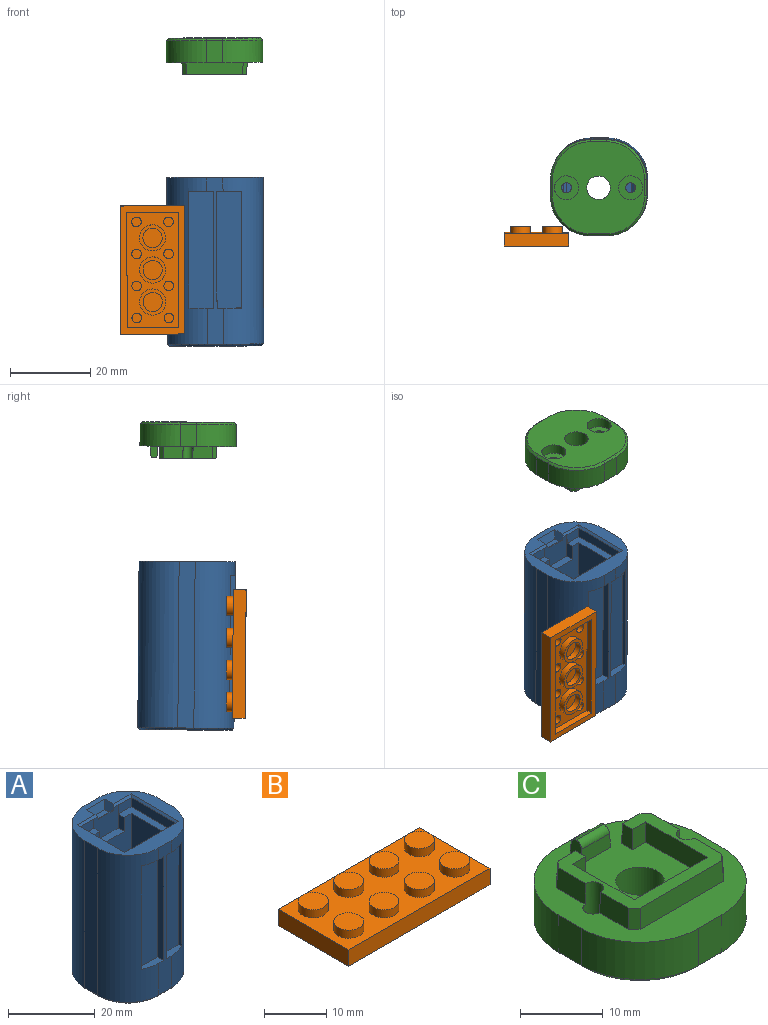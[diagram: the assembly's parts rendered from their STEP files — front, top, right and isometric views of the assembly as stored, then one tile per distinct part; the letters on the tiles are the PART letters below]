
ASSEMBLY  parts=3 mates=3
PART A: 128 faces, bbox 24x24x42 mm
  f0: plane 5.98x0.52mm, normal (0,-0.69,0.72), area 4mm2, adj f1,f112,f116,f118,f124
  f1: plane 24x24mm, normal (0,0,1), area 202.4mm2, adj f0,f2,f8,f9,f10,f13,f14,f15
  f2: plane 5.98x0.52mm, normal (0,-0.69,0.72), area 4mm2, adj f1,f4,f115,f118,f122
  f3: plane 27x12.5mm, normal (0,-1,0), area 305.5mm2, adj f5,f6,f53,f110,f119,f120,f121
  f4: plane 4.23x2.5mm, normal (0,-1,0.03), area 10.5mm2, adj f2,f110,f111,f120
  f5: plane 27x10.5mm, normal (-1,0,0), area 283.5mm2, adj f3,f7,f53,f110
  f6: plane 27x10.5mm, normal (1,0,0), area 283.5mm2, adj f3,f7,f53,f110
  f7: plane 27x12.5mm, normal (0,1,0), area 337.5mm2, adj f5,f6,f53,f110
  f8: plane 41.5x4mm, normal (0,-1,0), area 72.6mm2, adj f1,f9,f10,f57,f100,f101,f103,f105
  f9: cylinder r=10mm len=41.5mm, axis (0,0,-1), area 512.3mm2, adj f1,f8,f13,f59,f105,f106,f107
  f10: cylinder r=10mm len=41.5mm, axis (0,0,-1), area 512.3mm2, adj f1,f8,f17,f55,f100,f101,f102
  f11: cylinder r=2.65mm len=5.6mm, axis (0,0,-1), area 93.2mm2, adj f90,f98
  f12: cylinder r=2.65mm len=5.6mm, axis (0,0,-1), area 93.2mm2, adj f86,f99
  f13: plane 41.5x4mm, normal (1,0,0), area 166mm2, adj f1,f9,f14,f61
  f14: cylinder r=10mm len=41.5mm, axis (0,0,-1), area 651.9mm2, adj f1,f13,f15,f60
  f15: plane 41.5x4mm, normal (0,1,0), area 166mm2, adj f1,f14,f16,f58
  f16: cylinder r=10mm len=41.5mm, axis (0,0,-1), area 651.9mm2, adj f1,f15,f17,f56
  f17: plane 41.5x4mm, normal (-1,0,0), area 166mm2, adj f1,f10,f16,f54
  f18: plane 23x23mm, normal (0,0,-1), area 261.8mm2, adj f54,f55,f56,f57,f58,f59,f60,f61
  f19: cylinder r=0.1mm len=8.53mm, axis (0,0,-1), area 1.3mm2, adj f20,f34,f35,f80,f81
  f20: plane 8.5x1.21mm, normal (0,1,0), area 10.3mm2, adj f19,f21,f35,f80
  f21: cylinder r=2.65mm len=8.5mm, axis (0,0,-1), area 19.3mm2, adj f20,f22,f35,f62
  f22: plane 8.5x1.21mm, normal (0,-1,0), area 10.3mm2, adj f21,f23,f35,f85
  f23: cylinder r=0.1mm len=8.53mm, axis (0,0,-1), area 1.3mm2, adj f22,f24,f35,f84,f85
  f24: plane 8.5x1.21mm, normal (-1,0,0), area 10.3mm2, adj f23,f25,f35,f84
  f25: cylinder r=2.65mm len=8.5mm, axis (0,0,-1), area 19.3mm2, adj f24,f26,f35,f63
  f26: plane 8.5x1.21mm, normal (1,0,0), area 10.3mm2, adj f25,f27,f35,f82
  f27: cylinder r=0.1mm len=8.53mm, axis (0,0,-1), area 1.3mm2, adj f26,f28,f35,f82,f83
  f28: plane 8.5x1.21mm, normal (0,-1,0), area 10.3mm2, adj f27,f29,f35,f83
  f29: cylinder r=2.65mm len=8.5mm, axis (0,0,-1), area 19.3mm2, adj f28,f30,f35,f69
  f30: plane 8.5x1.21mm, normal (0,1,0), area 10.3mm2, adj f29,f31,f35,f78
  f31: cylinder r=0.1mm len=8.53mm, axis (0,0,-1), area 1.3mm2, adj f30,f32,f35,f78,f79
  f32: plane 8.5x1.21mm, normal (1,0,0), area 10.3mm2, adj f31,f33,f35,f79
  f33: cylinder r=2.65mm len=8.5mm, axis (0,0,-1), area 19.3mm2, adj f32,f34,f35,f64
  f34: plane 8.5x1.21mm, normal (-1,0,0), area 10.3mm2, adj f19,f33,f35,f81
  f35: plane 5.3x5.3mm, normal (0,0,-1), area 17.8mm2, adj f19,f20,f21,f22,f23,f24,f25,f26
  f36: cylinder r=0.1mm len=8.53mm, axis (0,0,-1), area 1.3mm2, adj f37,f51,f52,f72,f73
  f37: plane 8.5x1.21mm, normal (0,1,0), area 10.3mm2, adj f36,f38,f52,f73
  f38: cylinder r=2.65mm len=8.5mm, axis (0,0,-1), area 19.3mm2, adj f37,f39,f52,f68
  f39: plane 8.5x1.21mm, normal (0,-1,0), area 10.3mm2, adj f38,f40,f52,f71
  f40: cylinder r=0.1mm len=8.53mm, axis (0,0,-1), area 1.3mm2, adj f39,f41,f52,f70,f71
  f41: plane 8.5x1.21mm, normal (-1,0,0), area 10.3mm2, adj f40,f42,f52,f70
  f42: cylinder r=2.65mm len=8.5mm, axis (0,0,-1), area 19.3mm2, adj f41,f43,f52,f67
  f43: plane 8.5x1.21mm, normal (1,0,0), area 10.3mm2, adj f42,f44,f52,f76
  f44: cylinder r=0.1mm len=8.53mm, axis (0,0,-1), area 1.3mm2, adj f43,f45,f52,f76,f77
  f45: plane 8.5x1.21mm, normal (0,-1,0), area 10.3mm2, adj f44,f46,f52,f77
  f46: cylinder r=2.65mm len=8.5mm, axis (0,0,-1), area 19.3mm2, adj f45,f47,f52,f66
  f47: plane 8.5x1.21mm, normal (0,1,0), area 10.3mm2, adj f46,f48,f52,f74
  f48: cylinder r=0.1mm len=8.53mm, axis (0,0,-1), area 1.3mm2, adj f47,f49,f52,f74,f75
  f49: plane 8.5x1.21mm, normal (1,0,0), area 10.3mm2, adj f48,f50,f52,f75
  f50: cylinder r=2.65mm len=8.5mm, axis (0,0,-1), area 19.3mm2, adj f49,f51,f52,f65
  f51: plane 8.5x1.21mm, normal (-1,0,0), area 10.3mm2, adj f36,f50,f52,f72
  f52: plane 5.3x5.3mm, normal (0,0,-1), area 17.8mm2, adj f36,f37,f38,f39,f40,f41,f42,f43
  f53: plane 12.5x10.5mm, normal (0,0,1), area 63.3mm2, adj f3,f5,f6,f7,f97
  f54: plane 4x0.5mm, normal (-0.71,0,-0.71), area 2.8mm2, adj f17,f18,f55,f56
  f55: cone r=10mm half-angle=45deg, axis (0,0,1), area 10.8mm2, adj f10,f18,f54,f57
  f56: cone r=10mm half-angle=45deg, axis (0,0,1), area 10.8mm2, adj f16,f18,f54,f58
  f57: plane 4x0.5mm, normal (0,-0.71,-0.71), area 2.8mm2, adj f8,f18,f55,f59,f98
  f58: plane 4x0.5mm, normal (0,0.71,-0.71), area 2.8mm2, adj f15,f18,f56,f60,f99
  f59: cone r=10mm half-angle=45deg, axis (0,0,1), area 10.8mm2, adj f9,f18,f57,f61
  f60: cone r=10mm half-angle=45deg, axis (0,0,1), area 10.8mm2, adj f14,f18,f58,f61
  f61: plane 4x0.5mm, normal (0.71,0,-0.71), area 2.8mm2, adj f13,f18,f59,f60
  f62: cone r=2.65mm half-angle=45deg, axis (0,0,-1), area 2mm2, adj f18,f21,f80,f85
  f63: cone r=2.65mm half-angle=45deg, axis (0,0,-1), area 2mm2, adj f18,f25,f82,f84
  f64: cone r=2.65mm half-angle=45deg, axis (0,0,-1), area 2mm2, adj f18,f33,f79,f81
  f65: cone r=3.15mm half-angle=45deg, axis (0,0,-1), area 2mm2, adj f18,f50,f72,f75
  f66: cone r=3.15mm half-angle=45deg, axis (0,0,-1), area 2mm2, adj f18,f46,f74,f77
  f67: cone r=3.15mm half-angle=45deg, axis (0,0,-1), area 2mm2, adj f18,f42,f70,f76
  f68: cone r=3.15mm half-angle=45deg, axis (0,0,-1), area 2mm2, adj f18,f38,f71,f73
  f69: cone r=2.65mm half-angle=45deg, axis (0,0,-1), area 2mm2, adj f18,f29,f78,f83
  f70: plane 1.6x0.51mm, normal (-0.71,0,-0.71), area 0.9mm2, adj f18,f40,f41,f67,f71
  f71: plane 1.6x0.51mm, normal (0,-0.71,-0.71), area 0.9mm2, adj f18,f39,f40,f68,f70
  f72: plane 1.6x0.51mm, normal (-0.71,0,-0.71), area 0.9mm2, adj f18,f36,f51,f65,f73
  f73: plane 1.6x0.51mm, normal (0,0.71,-0.71), area 0.9mm2, adj f18,f36,f37,f68,f72
  f74: plane 1.6x0.51mm, normal (0,0.71,-0.71), area 0.9mm2, adj f18,f47,f48,f66,f75
  f75: plane 1.6x0.51mm, normal (0.71,0,-0.71), area 0.9mm2, adj f18,f48,f49,f65,f74
  f76: plane 1.6x0.51mm, normal (0.71,0,-0.71), area 0.9mm2, adj f18,f43,f44,f67,f77
  f77: plane 1.6x0.51mm, normal (0,-0.71,-0.71), area 0.9mm2, adj f18,f44,f45,f66,f76
  f78: plane 1.6x0.51mm, normal (0,0.71,-0.71), area 0.9mm2, adj f18,f30,f31,f69,f79
  f79: plane 1.6x0.51mm, normal (0.71,0,-0.71), area 0.9mm2, adj f18,f31,f32,f64,f78
  f80: plane 1.6x0.51mm, normal (0,0.71,-0.71), area 0.9mm2, adj f18,f19,f20,f62,f81
  f81: plane 1.6x0.51mm, normal (-0.71,0,-0.71), area 0.9mm2, adj f18,f19,f34,f64,f80
  f82: plane 1.6x0.51mm, normal (0.71,0,-0.71), area 0.9mm2, adj f18,f26,f27,f63,f83
  f83: plane 1.6x0.51mm, normal (0,-0.71,-0.71), area 0.9mm2, adj f18,f27,f28,f69,f82
  f84: plane 1.6x0.51mm, normal (-0.71,0,-0.71), area 0.9mm2, adj f18,f23,f24,f63,f85
  f85: plane 1.6x0.51mm, normal (0,-0.71,-0.71), area 0.9mm2, adj f18,f22,f23,f62,f84
  f86: plane 6.7x6.7mm, normal (0,0,1), area 13.2mm2, adj f12,f87
  f87: cylinder r=3.35mm len=6.7mm, axis (0,0,-1), area 10.5mm2, adj f86,f96
  f88: plane 5.3x5.3mm, normal (0,0,-1), area 22.1mm2, adj f89
  f89: cylinder r=2.65mm len=5.3mm, axis (0,0,-1), area 21.6mm2, adj f88,f96
  f90: plane 6.7x6.7mm, normal (0,0,1), area 13.2mm2, adj f11,f91
  f91: cylinder r=3.35mm len=6.7mm, axis (0,0,-1), area 10.5mm2, adj f90,f95
  f92: plane 5.3x5.3mm, normal (0,0,-1), area 22.1mm2, adj f93
  f93: cylinder r=2.65mm len=5.3mm, axis (0,0,-1), area 21.6mm2, adj f92,f95
  f94: cylinder r=4.15mm len=11.5mm, axis (0,0,-1), area 299.9mm2, adj f18,f97
  f95: cone r=2.35mm half-angle=45deg, axis (0,0,-1), area 18.7mm2, adj f91,f93
  f96: cone r=3.35mm half-angle=45deg, axis (0,0,-1), area 18.7mm2, adj f87,f89
  f97: cone r=4.65mm half-angle=45deg, axis (0,0,1), area 19.5mm2, adj f53,f94
  f98: cone r=2.65mm half-angle=45deg, axis (0,0,-1), area 24.8mm2, adj f11,f18,f57
  f99: cone r=2.65mm half-angle=45deg, axis (0,0,-1), area 24.8mm2, adj f12,f18,f58
  f100: plane 6.2x2mm, normal (0,0,1), area 10.7mm2, adj f8,f10,f102,f103,f104
  f101: plane 6.2x2mm, normal (0,0,-1), area 10.7mm2, adj f8,f10,f102,f103,f104
  f102: plane 29.2x0.88mm, normal (1,0,0), area 25.7mm2, adj f10,f100,f101,f104
  f103: plane 29.2x2mm, normal (-1,0,0), area 58.4mm2, adj f8,f100,f101,f104
  f104: plane 29.2x6.2mm, normal (0,-1,0), area 181mm2, adj f100,f101,f102,f103
  f105: plane 6.2x2mm, normal (0,0,-1), area 10.7mm2, adj f8,f9,f107,f108,f109
  f106: plane 6.2x2mm, normal (0,0,1), area 10.7mm2, adj f8,f9,f107,f108,f109
  f107: plane 29.2x0.88mm, normal (-1,0,0), area 25.7mm2, adj f9,f105,f106,f109
  f108: plane 29.2x2mm, normal (1,0,0), area 58.4mm2, adj f8,f105,f106,f109
  f109: plane 29.2x6.2mm, normal (0,-1,0), area 181mm2, adj f105,f106,f107,f108
  f110: plane 16.29x14.29mm, normal (0,0,1), area 86.4mm2, adj f3,f4,f5,f6,f7,f111,f112,f113
  f111: plane 14.47x2.5mm, normal (-1,0,0.03), area 36mm2, adj f4,f110,f114,f115
  f112: plane 4.23x2.5mm, normal (0,-1,0.03), area 10.5mm2, adj f0,f110,f113,f119
  f113: plane 14.47x2.5mm, normal (1,0,0.03), area 36mm2, adj f110,f112,f114,f116
  f114: plane 16.47x2.5mm, normal (0,1,0.03), area 41mm2, adj f110,f111,f113,f117
  f115: plane 15.5x0.52mm, normal (-0.69,0,0.72), area 10.8mm2, adj f1,f2,f111,f117
  f116: plane 15.5x0.52mm, normal (0.69,0,0.72), area 10.8mm2, adj f0,f1,f113,f117
  f117: plane 17.5x0.52mm, normal (0,0.69,0.72), area 12.2mm2, adj f1,f114,f115,f116
  f118: plane 8x6.5mm, normal (0,-1,0), area 48.1mm2, adj f0,f2,f119,f120,f121,f122,f124,f127
  f119: plane 6.5x1.98mm, normal (1,0,0), area 8mm2, adj f3,f110,f112,f118,f121
  f120: plane 6.5x1.98mm, normal (-1,0,0), area 8mm2, adj f3,f4,f110,f118,f121
  f121: plane 8x1.98mm, normal (0,0,1), area 15.9mm2, adj f3,f118,f119,f120
  f122: plane 3.27x2mm, normal (-0.91,0,0.42), area 5.7mm2, adj f1,f2,f118,f123,f125,f126,f127
  f123: plane 6x2mm, normal (0,-0.91,0.42), area 11.2mm2, adj f1,f122,f124,f126
  f124: plane 3.27x2mm, normal (0.91,0,0.42), area 5.7mm2, adj f0,f1,f118,f123,f125,f126,f127
  f125: plane 4.35x0.23mm, normal (0,0.91,0.42), area 1.1mm2, adj f122,f124,f126,f127
  f126: plane 4.13x1.63mm, normal (0,0,1), area 6.8mm2, adj f122,f123,f124,f125
  f127: cylinder r=1mm len=4.84mm, axis (1,0,0), area 3.8mm2, adj f118,f122,f124,f125
PART B: 55 faces, bbox 32x16x4.8 mm
  f0: plane 4.8x4.8mm, normal (0,0,-1), area 18.1mm2, adj f2
  f1: plane 4.8x4.8mm, normal (0,0,-1), area 18.1mm2, adj f5
  f2: cylinder r=2.4mm len=4.8mm, axis (0,0,1), area 24.1mm2, adj f0,f4
  f3: cylinder r=3.26mm len=6.51mm, axis (0,0,1), area 32.7mm2, adj f4,f18
  f4: plane 6.51x6.51mm, normal (0,0,-1), area 15.2mm2, adj f2,f3
  f5: cylinder r=2.4mm len=4.8mm, axis (0,0,1), area 24.1mm2, adj f1,f7
  f6: cylinder r=3.26mm len=6.51mm, axis (0,0,1), area 32.7mm2, adj f7,f18
  f7: plane 6.51x6.51mm, normal (0,0,-1), area 15.2mm2, adj f5,f6
  f8: plane 32x16mm, normal (0,0,-1), area 143.4mm2, adj f9,f10,f11,f12,f14,f15,f16,f17
  f9: plane 16x3.2mm, normal (-1,0,0), area 51.2mm2, adj f8,f10,f12,f13
  f10: plane 32x3.2mm, normal (0,-1,0), area 102.4mm2, adj f8,f9,f11,f13
  f11: plane 16x3.2mm, normal (1,0,0), area 51.2mm2, adj f8,f10,f12,f13
  f12: plane 32x3.2mm, normal (0,1,0), area 102.4mm2, adj f8,f9,f11,f13
  f13: plane 32x16mm, normal (0,0,1), area 367.2mm2, adj f9,f10,f11,f12,f19,f21,f23,f25
  f14: plane 12.8x1.6mm, normal (1,0,0), area 20.5mm2, adj f8,f15,f17,f18
  f15: plane 28.8x1.6mm, normal (0,-1,0), area 46.1mm2, adj f8,f14,f16,f18
  f16: plane 12.8x1.6mm, normal (-1,0,0), area 20.5mm2, adj f8,f15,f17,f18
  f17: plane 28.8x1.6mm, normal (0,1,0), area 46.1mm2, adj f8,f14,f16,f18
  f18: plane 28.8x12.8mm, normal (0,0,-1), area 232.5mm2, adj f3,f6,f14,f15,f16,f17,f35,f37
  f19: cylinder r=2.4mm len=4.8mm, axis (0,0,-1), area 24.1mm2, adj f13,f20
  f20: plane 4.8x4.8mm, normal (0,0,1), area 18.1mm2, adj f19
  f21: cylinder r=2.4mm len=4.8mm, axis (0,0,-1), area 24.1mm2, adj f13,f22
  f22: plane 4.8x4.8mm, normal (0,0,1), area 18.1mm2, adj f21
  f23: cylinder r=2.4mm len=4.8mm, axis (0,0,-1), area 24.1mm2, adj f13,f24
  f24: plane 4.8x4.8mm, normal (0,0,1), area 18.1mm2, adj f23
  f25: cylinder r=2.4mm len=4.8mm, axis (0,0,-1), area 24.1mm2, adj f13,f26
  f26: plane 4.8x4.8mm, normal (0,0,1), area 18.1mm2, adj f25
  f27: cylinder r=2.4mm len=4.8mm, axis (0,0,-1), area 24.1mm2, adj f13,f28
  f28: plane 4.8x4.8mm, normal (0,0,1), area 18.1mm2, adj f27
  f29: cylinder r=2.4mm len=4.8mm, axis (0,0,-1), area 24.1mm2, adj f13,f30
  f30: plane 4.8x4.8mm, normal (0,0,1), area 18.1mm2, adj f29
  f31: cylinder r=2.4mm len=4.8mm, axis (0,0,-1), area 24.1mm2, adj f13,f32
  f32: plane 4.8x4.8mm, normal (0,0,1), area 18.1mm2, adj f31
  f33: cylinder r=2.4mm len=4.8mm, axis (0,0,-1), area 24.1mm2, adj f13,f34
  f34: plane 4.8x4.8mm, normal (0,0,1), area 18.1mm2, adj f33
  f35: cylinder r=1.2mm len=2.4mm, axis (0,0,-1), area 12.1mm2, adj f18,f36
  f36: plane 2.4x2.4mm, normal (0,0,-1), area 4.5mm2, adj f35
  f37: cylinder r=1.2mm len=2.4mm, axis (0,0,-1), area 12.1mm2, adj f18,f38
  f38: plane 2.4x2.4mm, normal (0,0,-1), area 4.5mm2, adj f37
  f39: cylinder r=1.2mm len=2.4mm, axis (0,0,-1), area 12.1mm2, adj f18,f40
  f40: plane 2.4x2.4mm, normal (0,0,-1), area 4.5mm2, adj f39
  f41: cylinder r=1.2mm len=2.4mm, axis (0,0,-1), area 12.1mm2, adj f18,f42
  f42: plane 2.4x2.4mm, normal (0,0,-1), area 4.5mm2, adj f41
  f43: cylinder r=1.2mm len=2.4mm, axis (0,0,-1), area 12.1mm2, adj f18,f44
  f44: plane 2.4x2.4mm, normal (0,0,-1), area 4.5mm2, adj f43
  f45: cylinder r=1.2mm len=2.4mm, axis (0,0,-1), area 12.1mm2, adj f18,f46
  f46: plane 2.4x2.4mm, normal (0,0,-1), area 4.5mm2, adj f45
  f47: cylinder r=1.2mm len=2.4mm, axis (0,0,-1), area 12.1mm2, adj f18,f48
  f48: plane 2.4x2.4mm, normal (0,0,-1), area 4.5mm2, adj f47
  f49: cylinder r=1.2mm len=2.4mm, axis (0,0,-1), area 12.1mm2, adj f18,f50
  f50: plane 2.4x2.4mm, normal (0,0,-1), area 4.5mm2, adj f49
  f51: cylinder r=2.4mm len=4.8mm, axis (0,0,1), area 24.1mm2, adj f53,f54
  f52: cylinder r=3.26mm len=6.51mm, axis (0,0,1), area 32.7mm2, adj f18,f53
  f53: plane 6.51x6.51mm, normal (0,0,-1), area 15.2mm2, adj f51,f52
  f54: plane 4.8x4.8mm, normal (0,0,-1), area 18.1mm2, adj f51
PART C: 50 faces, bbox 24x24x9 mm
  f0: plane 4.91x3.01mm, normal (-1,0,0.05), area 14.5mm2, adj f2,f4,f41,f45
  f1: plane 4.91x3.01mm, normal (1,0,0.05), area 14.5mm2, adj f2,f4,f38,f42
  f2: plane 15.99x13.99mm, normal (0,0,1), area 71.5mm2, adj f0,f1,f3,f23,f24,f25,f26,f31
  f3: plane 3.15x3mm, normal (0,1,0.05), area 9.2mm2, adj f2,f4,f32,f40
  f4: plane 24x24mm, normal (0,0,1), area 364mm2, adj f0,f1,f3,f5,f6,f7,f8,f9
  f5: plane 5.5x4mm, normal (0,-1,0), area 22mm2, adj f4,f6,f13,f18
  f6: cylinder r=10mm len=10mm, axis (0,0,-1), area 86.4mm2, adj f4,f5,f7,f20
  f7: plane 5.5x4mm, normal (1,0,0), area 22mm2, adj f4,f6,f8,f22
  f8: cylinder r=10mm len=10mm, axis (0,0,-1), area 86.4mm2, adj f4,f7,f9,f21
  f9: plane 5.5x4mm, normal (0,1,0), area 22mm2, adj f4,f8,f10,f19
  f10: cylinder r=10mm len=10mm, axis (0,0,-1), area 86.4mm2, adj f4,f9,f11,f17
  f11: plane 5.5x4mm, normal (-1,0,0), area 22mm2, adj f4,f10,f13,f15
  f12: cylinder r=2.95mm len=6mm, axis (0,0,-1), area 111.2mm2, adj f4,f14
  f13: cylinder r=10mm len=10mm, axis (0,0,-1), area 86.4mm2, adj f4,f5,f11,f16
  f14: plane 23x23mm, normal (0,0,-1), area 367.6mm2, adj f12,f15,f16,f17,f18,f19,f20,f21
  f15: plane 4x0.5mm, normal (-0.71,0,-0.71), area 2.8mm2, adj f11,f14,f16,f17
  f16: cone r=10mm half-angle=45deg, axis (0,0,1), area 10.8mm2, adj f13,f14,f15,f18
  f17: cone r=10mm half-angle=45deg, axis (0,0,1), area 10.8mm2, adj f10,f14,f15,f19
  f18: plane 4x0.5mm, normal (0,-0.71,-0.71), area 2.8mm2, adj f5,f14,f16,f20
  f19: plane 4x0.5mm, normal (0,0.71,-0.71), area 2.8mm2, adj f9,f14,f17,f21
  f20: cone r=10mm half-angle=45deg, axis (0,0,1), area 10.8mm2, adj f6,f14,f18,f22
  f21: cone r=10mm half-angle=45deg, axis (0,0,1), area 10.8mm2, adj f8,f14,f19,f22
  f22: plane 4x0.5mm, normal (0.71,0,-0.71), area 2.8mm2, adj f7,f14,f20,f21
  f23: plane 14.3x3mm, normal (0,-1,0.05), area 42.5mm2, adj f2,f4,f38,f41
  f24: plane 4.91x3.01mm, normal (-1,0,0.05), area 14.5mm2, adj f2,f4,f40,f45
  f25: plane 3.15x3mm, normal (0,1,0.05), area 9.2mm2, adj f2,f4,f31,f39
  f26: plane 4.91x3.01mm, normal (1,0,0.05), area 14.5mm2, adj f2,f4,f39,f42
  f27: plane 3.01x2.02mm, normal (1,0,0.05), area 5.2mm2, adj f4,f28,f30,f48,f49
  f28: plane 5x2.05mm, normal (0,1,0.05), area 10.1mm2, adj f4,f27,f29,f49
  f29: plane 3.01x2.02mm, normal (-1,0,0.05), area 5.2mm2, adj f4,f28,f30,f48,f49
  f30: plane 5x2.05mm, normal (0,-1,0.05), area 10.1mm2, adj f4,f27,f29,f48
  f31: plane 3x1.9mm, normal (-1,0,0), area 5.5mm2, adj f2,f4,f25,f37
  f32: plane 3x1.9mm, normal (1,0,0), area 5.5mm2, adj f2,f3,f4,f33
  f33: plane 3x2.25mm, normal (0,-1,0), area 6.7mm2, adj f2,f4,f32,f34
  f34: plane 10.5x3mm, normal (1,0,0), area 31.5mm2, adj f2,f4,f33,f35
  f35: plane 12.5x3mm, normal (0,1,0), area 37.5mm2, adj f2,f4,f34,f36
  f36: plane 10.5x3mm, normal (-1,0,0), area 31.5mm2, adj f2,f4,f35,f37
  f37: plane 3x2.25mm, normal (0,-1,0), area 6.7mm2, adj f2,f4,f31,f36
  f38: plane 3x1.16mm, normal (0.71,-0.71,0.07), area 4.3mm2, adj f1,f2,f4,f23
  f39: plane 3x1.16mm, normal (0.71,0.71,0.07), area 4.3mm2, adj f2,f4,f25,f26
  f40: plane 3x1.16mm, normal (-0.71,0.71,0.07), area 4.3mm2, adj f2,f3,f4,f24
  f41: plane 3x1.16mm, normal (-0.71,-0.71,0.07), area 4.3mm2, adj f0,f2,f4,f23
  f42: cylinder r=1.25mm len=6.5mm, axis (0,0,-1), area 39.7mm2, adj f1,f2,f4,f26,f43
  f43: plane 6x6mm, normal (0,0,-1), area 23.4mm2, adj f42,f44
  f44: cylinder r=3mm len=6mm, axis (0,0,-1), area 47.1mm2, adj f14,f43
  f45: cylinder r=1.25mm len=6.5mm, axis (0,0,-1), area 39.7mm2, adj f0,f2,f4,f24,f46
  f46: plane 6x6mm, normal (0,0,-1), area 23.4mm2, adj f45,f47
  f47: cylinder r=3mm len=6mm, axis (0,0,-1), area 47.1mm2, adj f14,f46
  f48: cylinder r=1mm len=4.79mm, axis (-1,0,0), area 6.7mm2, adj f27,f29,f30,f49
  f49: cylinder r=1mm len=4.79mm, axis (-1,0,0), area 6.7mm2, adj f27,f28,f29,f48
PLACE A rot(axis=(0.9,-0.42,-0.08),0.5deg) t=(16.6,2.58,-40.82)mm
PLACE B rot(axis=(-0.58,0.58,0.58),119.6deg) t=(0.88,-12.36,-21.9)mm
PLACE C rot(axis=(0,1,0),179.8deg) t=(16.32,1.98,35.97)mm
MATE slider C.f12 <-> A.f94  axis (0,0.01,-1) through (16.34,2.03,29.97)mm
MATE parallel A.f104 <-> B.f21  axis (0,-1,-0.01) through (13.01,-7.6,-16.81)mm
MATE parallel C.f12 <-> A.f1  axis (0,0.01,-1) through (16.34,2.03,29.97)mm
